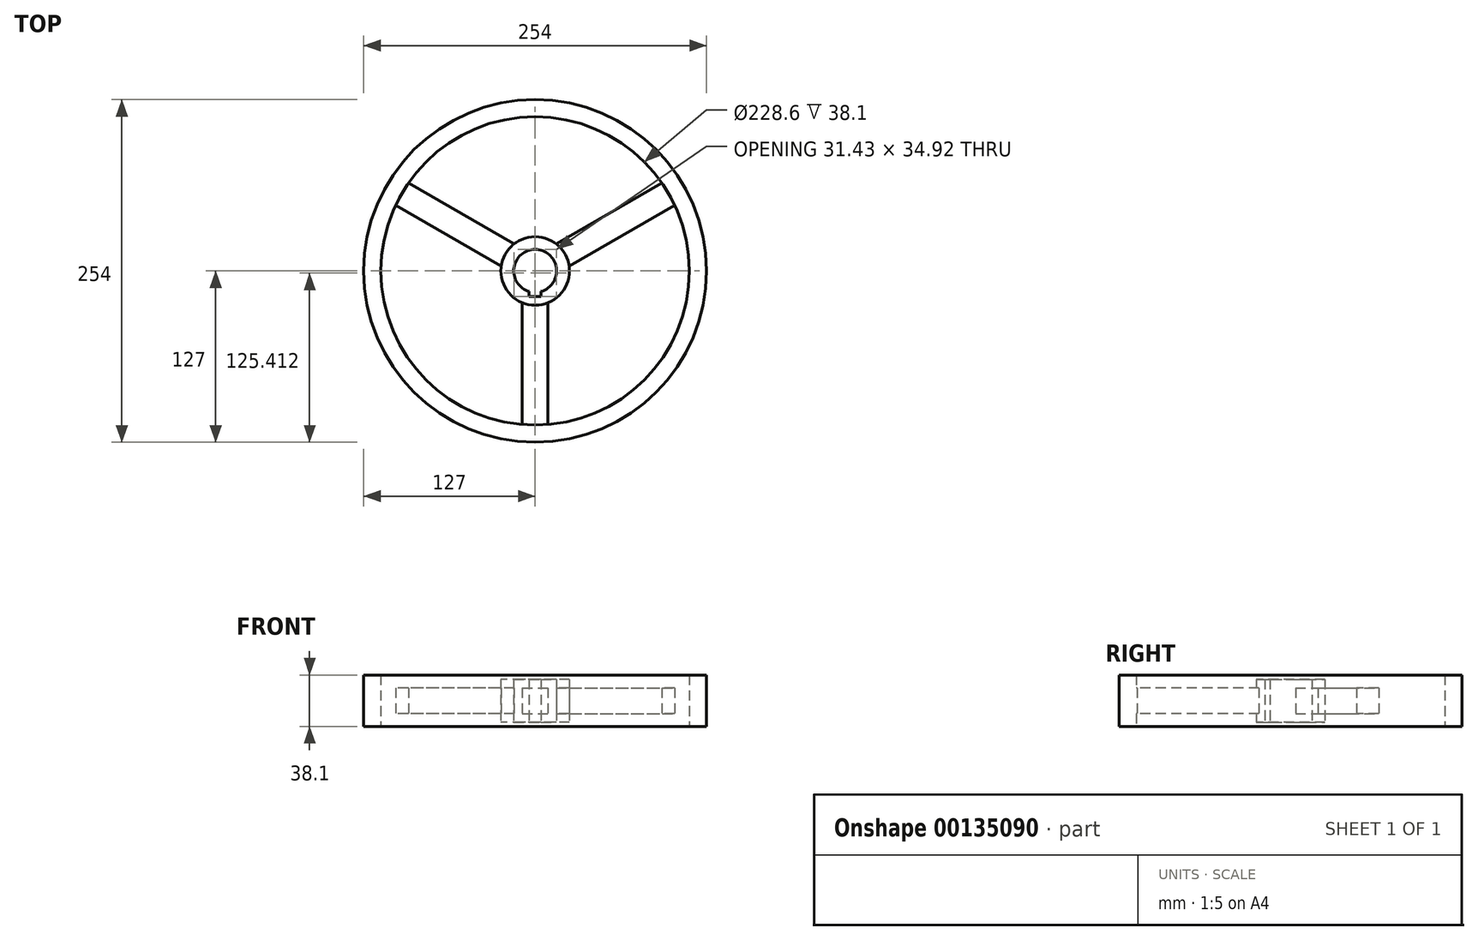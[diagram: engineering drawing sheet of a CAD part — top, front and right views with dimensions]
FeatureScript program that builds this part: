
annotation { "Feature Type Name" : "Feature", "Feature Type Description" : "" }
export const myFeature = defineFeature(function(context is Context, id is Id, definition is map)
    precondition{}
    {
        {
            var Q0;
            Q0=qCreatedBy(makeId("Top.planeOp"),FACE);
            var sketch = newSketch(context, id + "F0", { "sketchPlane" : qUnion([Q0])});
            skCircle(sketch, "E0", {"center": v(0, 0) * mm, "radius": 25.4 * mm});
            skArc(sketch, "E1", {"start": v(4.45, -15.24) * mm, "mid": v(0, 15.88) * mm, "end": v(-4.45, -15.24) * mm});
            skLineSegment(sketch, "E2", {"start": v(0, 0) * mm, "end": v(0, -19.05) * mm, "construction": true});
            skLineSegment(sketch, "E3", {"start": v(-4.44, -19.05) * mm, "end": v(4.44, -19.05) * mm});
            skLineSegment(sketch, "E4", {"start": v(-4.44, -19.05) * mm, "end": v(-4.44, -15.24) * mm});
            skLineSegment(sketch, "E5.MirrorCS", {"start": v(4.44, -19.05) * mm, "end": v(4.44, -15.24) * mm});
            skCircle(sketch, "E6", {"center": v(0, 0) * mm, "radius": 114.3 * mm});
            skCircle(sketch, "E7", {"center": v(0, 0) * mm, "radius": 127 * mm});
            skLineSegment(sketch, "E8", {"start": v(0, -25.4) * mm, "end": v(0, -114.3) * mm, "construction": true});
            skLineSegment(sketch, "E9.0", {"start": v(-9.53, -23.55) * mm, "end": v(-9.52, -113.9) * mm});
            skLineSegment(sketch, "E10.MirrorCS", {"start": v(9.53, -23.55) * mm, "end": v(9.52, -113.9) * mm});
            skLineSegment(sketch, "E11.1.0", {"start": v(25.15, 3.52) * mm, "end": v(103.4, 48.7) * mm});
            skLineSegment(sketch, "E11.1.1", {"start": v(15.63, 20.02) * mm, "end": v(93.88, 65.2) * mm});
            skLineSegment(sketch, "E11.2.0", {"start": v(-15.63, 20.02) * mm, "end": v(-93.88, 65.2) * mm});
            skLineSegment(sketch, "E11.2.1", {"start": v(-25.15, 3.52) * mm, "end": v(-103.4, 48.7) * mm});
            skSolve(sketch);
        }
        {
            var Q0;
            Q0=makeQuery(id+"F0.imprint","IMPRINT",FACE,{"disambiguationData":[TD([[makeQuery(id+"F0.imprint","IMPRINT",EDGE,{"derivedFrom":sQuery(id+"F0.wireOp",EDGE,"E7")}),1.0]])]});
            extrude(context, id + "F1", {"entities" : qUnion([Q0]), "depth" : 19.05 * mm, "hasSecondDirection" : true, "secondDirectionOppositeDirection" : true, "secondDirectionDepth" : 19.05 * mm});
        }
        {
            var Q0;
            {var subQ0=sQuery(id+"F0.wireOp",EDGE,"E9.0");Q0=makeQuery(id+"F0.imprint","IMPRINT",FACE,{"disambiguationData":[TD([[makeQuery(id+"F0.imprint","IMPRINT",EDGE,{"derivedFrom":subQ0}),1.0]])]});}
            var Q1;
            {var subQ0=sQuery(id+"F0.wireOp",EDGE,"E11.2.0");Q1=makeQuery(id+"F0.imprint","IMPRINT",FACE,{"disambiguationData":[TD([[makeQuery(id+"F0.imprint","IMPRINT",EDGE,{"derivedFrom":subQ0}),1.0]])]});}
            var Q2;
            {var subQ0=sQuery(id+"F0.wireOp",EDGE,"E11.1.0");Q2=makeQuery(id+"F0.imprint","IMPRINT",FACE,{"disambiguationData":[TD([[makeQuery(id+"F0.imprint","IMPRINT",EDGE,{"derivedFrom":subQ0}),1.0]])]});}
            extrude(context, id + "F2", {"entities" : qUnion([Q0, Q1, Q2]), "operationType" : NewBodyOperationType.ADD, "depth" : 9.52 * mm, "hasSecondDirection" : true, "secondDirectionOppositeDirection" : true, "secondDirectionDepth" : 9.52 * mm});
        }
        {
            var Q0;
            Q0=makeQuery(id+"F0.imprint","IMPRINT",FACE,{"disambiguationData":[TD([[makeQuery(id+"F0.imprint","IMPRINT",EDGE,{"derivedFrom":sQuery(id+"F0.wireOp",EDGE,"E1")}),-1.0]])]});
            extrude(context, id + "F3", {"entities" : qUnion([Q0]), "operationType" : NewBodyOperationType.ADD, "depth" : 15.88 * mm, "hasSecondDirection" : true, "secondDirectionOppositeDirection" : true, "secondDirectionDepth" : 15.88 * mm});
        }
    });
